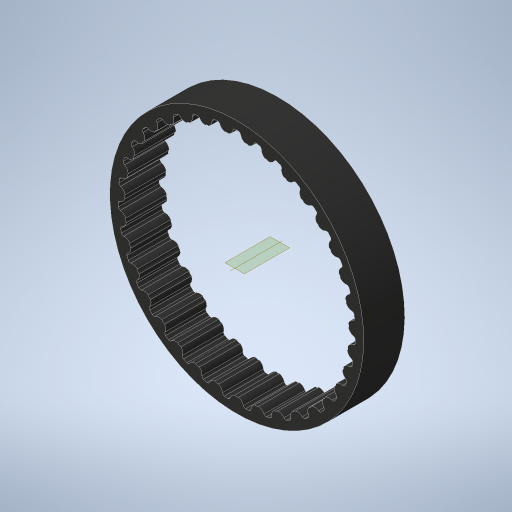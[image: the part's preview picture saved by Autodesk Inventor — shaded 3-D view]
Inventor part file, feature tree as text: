
AUTODESK INVENTOR PART (.ipt)
format: ipt  version: 2023.3 (Build 273359000, 359)  size: 782,336 bytes
history: native  units: in
note: dims shown in document units (in); Inventor stores cm internally (conversion verified against a paired STEP export)
features: extrude x3, sketch x3, projected_geometry x3, plane x1, other x1, pattern_circular x1
ambient origin geometry x8: Origin, YZ Plane, XZ Plane, XY Plane, X Axis, Y Axis, Z Axis, Center Point
bodies: Solid1 (feature_tree)
feature tree (12):
  extrude  "Extrusion1"  Depth=0.0197in
  plane  "Work Plane1"
  sketch  "Sketch2"  dims[d3=0.0591in]
  other  "Work Axis1"
  pattern_circular  "Circular Pattern1"  [2 undecoded]
  sketch  "Sketch3"  dims[d4=0.0328in d5=0.0591in d6=0.0197in d7=0.0748in d8=0.0945in d9=0.0762in d10=0.0762in d11=0.0655in d12=0.0197in d13=0.0748in d14=0.0in d15=0.25in d16=0.0191in d17=0.0408in d18=0.0148in d19=0.042in d20=0.3543in d21=0.0in d22=-1.0965in d23=13.7795in d24=360.0deg d26=2.1931in d27=0.125in d28=0.0in d29=0.0in d30=1.0in d31=0.0in]
  extrude  "Extrusion2"  Depth=0.0197in
  extrude  "Extrusion3"  Depth=0.3543in
  sketch  "Sketch1"  dims[d1=0.0444in d2=0.0197in]
  projected_geometry  "Projected Loop1"
  projected_geometry  "Project Cut Edges1"
  projected_geometry  "Project Cut Edges2"
note: 2 required parameter values undecoded (feature->parameter linkage not recoverable at this tier; creation-order binding heuristic only, values carry confidence <= 0.55)
